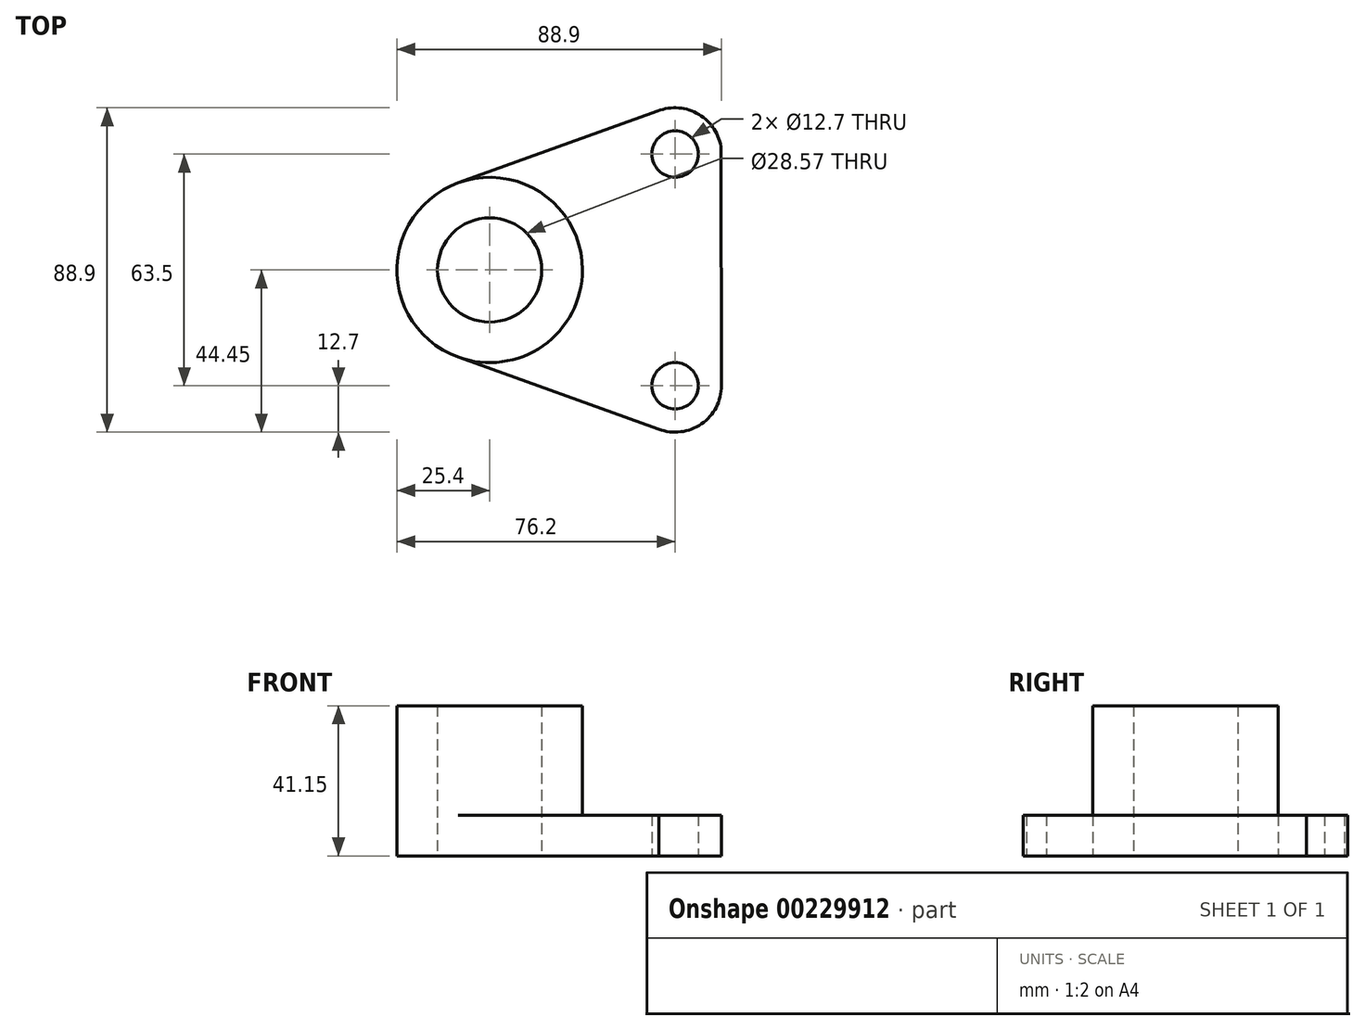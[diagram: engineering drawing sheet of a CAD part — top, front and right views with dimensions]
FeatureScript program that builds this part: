
annotation { "Feature Type Name" : "Feature", "Feature Type Description" : "" }
export const myFeature = defineFeature(function(context is Context, id is Id, definition is map)
    precondition{}
    {
        {
            var Q0;
            Q0=qCreatedBy(makeId("Top.planeOp"),FACE);
            var sketch = newSketch(context, id + "F0", { "sketchPlane" : qUnion([Q0])});
            skCircle(sketch, "E0", {"center": v(0, 0) * mm, "radius": 14.29 * mm});
            skCircle(sketch, "E1", {"center": v(0, 0) * mm, "radius": 25.4 * mm});
            skLineSegment(sketch, "E2", {"start": v(0, 0) * mm, "end": v(50.8, 0) * mm});
            skLineSegment(sketch, "E3", {"start": v(50.8, 0) * mm, "end": v(50.8, 31.75) * mm});
            skLineSegment(sketch, "E4", {"start": v(50.8, 0) * mm, "end": v(50.8, -31.75) * mm});
            skCircle(sketch, "E5", {"center": v(50.8, 31.75) * mm, "radius": 6.35 * mm});
            skCircle(sketch, "E6", {"center": v(50.8, -31.75) * mm, "radius": 6.35 * mm});
            skArc(sketch, "E7", {"start": v(63.43, 30.42) * mm, "mid": v(58.46, 41.88) * mm, "end": v(46.07, 43.54) * mm});
            skArc(sketch, "E8", {"start": v(46.32, -43.63) * mm, "mid": v(58.03, -42.2) * mm, "end": v(63.5, -31.74) * mm});
            skLineSegment(sketch, "E9", {"start": v(46.32, -43.63) * mm, "end": v(-8.59, -23.9) * mm});
            skLineSegment(sketch, "E10", {"start": v(46.07, 43.54) * mm, "end": v(-8.59, 23.9) * mm});
            skLineSegment(sketch, "E11", {"start": v(63.43, 33.11) * mm, "end": v(63.5, -31.74) * mm});
            skSolve(sketch);
        }
        {
            var Q0;
            Q0=makeQuery(id+"F0.imprint","IMPRINT",FACE,{"disambiguationData":[TD([[makeQuery(id+"F0.imprint","IMPRINT",EDGE,{"derivedFrom":sQuery(id+"F0.wireOp",EDGE,"E0")}),-1.0]])]});
            var Q1;
            Q1=makeQuery(id+"F0.imprint","IMPRINT",FACE,{"disambiguationData":[TD([[makeQuery(id+"F0.imprint","IMPRINT",EDGE,{"derivedFrom":sQuery(id+"F0.wireOp",EDGE,"E5")}),-1.0]])]});
            extrude(context, id + "F1", {"entities" : qUnion([Q0, Q1]), "depth" : 11.18 * mm});
        }
        {
            var Q0;
            Q0=makeQuery(id+"F0.imprint","IMPRINT",FACE,{"disambiguationData":[TD([[makeQuery(id+"F0.imprint","IMPRINT",EDGE,{"derivedFrom":sQuery(id+"F0.wireOp",EDGE,"E0")}),-1.0]])]});
            extrude(context, id + "F2", {"entities" : qUnion([Q0]), "operationType" : NewBodyOperationType.ADD, "depth" : 41.15 * mm});
        }
    });
